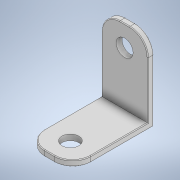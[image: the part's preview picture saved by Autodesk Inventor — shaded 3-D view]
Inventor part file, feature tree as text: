
AUTODESK INVENTOR PART (.ipt)
format: ipt  version: 2022.1 (Build 261234020, 234B)  size: 169,984 bytes
history: native  units: in
note: dims shown in document units (in); Inventor stores cm internally (conversion verified against a paired STEP export)
features: sketch x4, extrude x3, fillet x3
ambient origin geometry x8: Origin, YZ Plane, XZ Plane, XY Plane, X Axis, Y Axis, Z Axis, Center Point
bodies: Solid1 (feature_tree)
feature tree (10):
  sketch  "Sketch1"  dims[d0=0.635in d1=1.11in]
  extrude  "Extrusion1"  Depth=1.11in
  extrude  "Extrusion2"  Depth=0.079in
  fillet  "Fillet1"  Radius=0.079in
  sketch  "Sketch4"  dims[d12=0.286in d13=0.25in d14=0.079in d15=0.0in d16=0.01in d17=0.0in d18=0.0in d19=0.0in]
  fillet  "Fillet2"  Radius=0.079in
  extrude  "Extrusion3"  Depth=0.25in
  fillet  "Fillet3"  Radius=0.232in
  sketch  "Sketch2"  dims[d3=0.232in d4=0.286in d5=0.079in d6=0.0in d7=0.079in]
  sketch  "Sketch3"  dims[d8=1.1in d9=0.0in d10=0.25in d11=0.232in]
